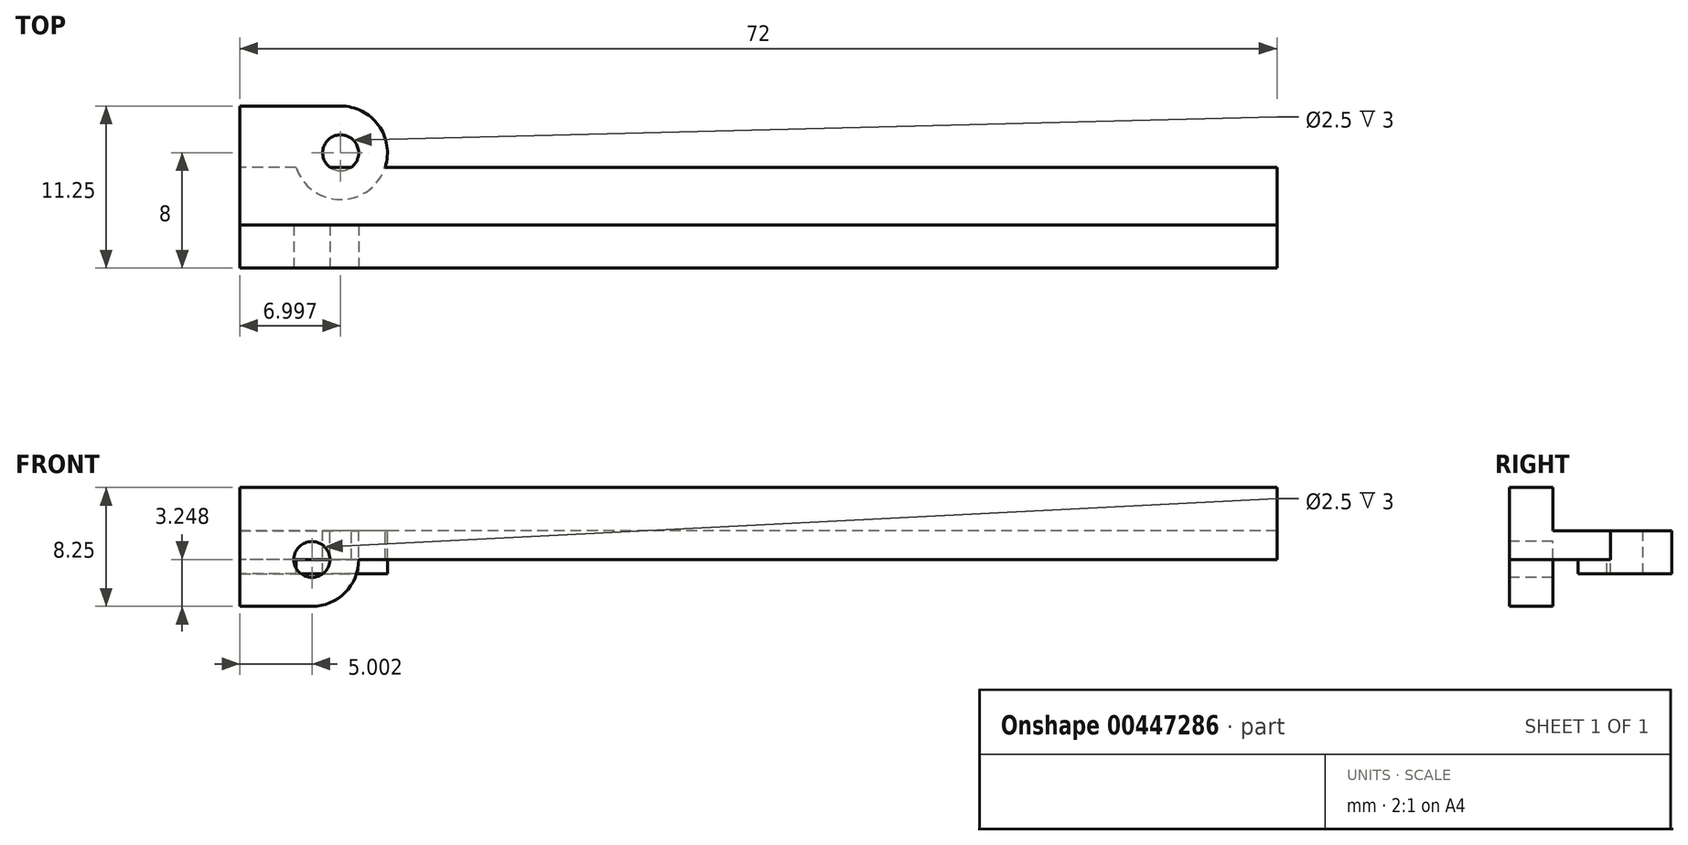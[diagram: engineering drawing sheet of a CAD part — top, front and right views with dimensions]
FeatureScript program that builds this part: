
annotation { "Feature Type Name" : "Feature", "Feature Type Description" : "" }
export const myFeature = defineFeature(function(context is Context, id is Id, definition is map)
    precondition{}
    {
        {
            var Q0;
            Q0=qCreatedBy(makeId("Front.planeOp"),FACE);
            var sketch = newSketch(context, id + "F0", { "sketchPlane" : qUnion([Q0])});
            skLineSegment(sketch, "E0", {"start": v(-25.69, -103.36) * mm, "end": v(-25.69, 66.64) * mm, "construction": true});
            skLineSegment(sketch, "E1.bottom", {"start": v(-27.99, 69.24) * mm, "end": v(16.71, 69.24) * mm, "construction": true});
            skLineSegment(sketch, "E1.top", {"start": v(-27.99, -89.76) * mm, "end": v(16.71, -89.76) * mm, "construction": true});
            skLineSegment(sketch, "E1.left", {"start": v(-27.99, 69.24) * mm, "end": v(-27.99, -89.76) * mm, "construction": true});
            skLineSegment(sketch, "E1.right", {"start": v(16.71, 69.24) * mm, "end": v(16.71, -89.76) * mm, "construction": true});
            skLineSegment(sketch, "E2", {"start": v(-25.69, 66.64) * mm, "end": v(-25.69, 76.64) * mm, "construction": true});
            skLineSegment(sketch, "E3", {"start": v(-25.69, 76.64) * mm, "end": v(-38.69, 76.64) * mm});
            skLineSegment(sketch, "E4", {"start": v(-38.69, 76.64) * mm, "end": v(-38.69, 79.64) * mm});
            skLineSegment(sketch, "E5", {"start": v(-38.69, 79.64) * mm, "end": v(33.31, 79.64) * mm});
            skLineSegment(sketch, "E6", {"start": v(-33.69, 79.64) * mm, "end": v(-33.69, 74.64) * mm, "construction": true});
            skCircle(sketch, "E7", {"center": v(-33.69, 74.64) * mm, "radius": 1.25 * mm});
            skCircle(sketch, "E8", {"center": v(-33.69, 74.64) * mm, "radius": 3.25 * mm});
            skLineSegment(sketch, "E9", {"start": v(-33.69, 71.39) * mm, "end": v(-38.69, 71.39) * mm});
            skLineSegment(sketch, "E10", {"start": v(-38.69, 71.39) * mm, "end": v(-38.69, 76.64) * mm});
            skLineSegment(sketch, "E11", {"start": v(-25.69, 76.64) * mm, "end": v(33.31, 76.64) * mm});
            skLineSegment(sketch, "E12", {"start": v(33.31, 76.64) * mm, "end": v(33.31, 79.64) * mm});
            skLineSegment(sketch, "E13", {"start": v(33.31, 76.64) * mm, "end": v(33.31, 74.64) * mm});
            skLineSegment(sketch, "E14", {"start": v(33.31, 74.64) * mm, "end": v(-30.44, 74.64) * mm});
            skLineSegment(sketch, "E15", {"start": v(33.31, 74.64) * mm, "end": v(33.31, 72.64) * mm});
            skLineSegment(sketch, "E16", {"start": v(33.31, 72.64) * mm, "end": v(-31.13, 72.64) * mm});
            skSolve(sketch);
        }
        {
            var Q0;
            {var subQ0=sQuery(id+"F0.wireOp",EDGE,"E11");Q0=makeQuery(id+"F0.imprint","IMPRINT",FACE,{"disambiguationData":[TD([[makeQuery(id+"F0.imprint","IMPRINT",EDGE,{"derivedFrom":subQ0}),-1.0]])]});}
            var Q1;
            Q1=makeQuery(id+"F0.imprint","IMPRINT",FACE,{"disambiguationData":[TD([[makeQuery(id+"F0.imprint","IMPRINT",EDGE,{"derivedFrom":sQuery(id+"F0.wireOp",EDGE,"E7")}),-1.0]])]});
            var Q2;
            {var subQ4=sQuery(id+"F0.wireOp",EDGE,"E9");Q2=makeQuery(id+"F0.imprint","IMPRINT",FACE,{"disambiguationData":[TD([[makeQuery(id+"F0.imprint","IMPRINT",EDGE,{"derivedFrom":subQ4}),-1.0]])]});}
            var Q3;
            {var subQ0=sQuery(id+"F0.wireOp",EDGE,"E4");Q3=makeQuery(id+"F0.imprint","IMPRINT",FACE,{"disambiguationData":[TD([[makeQuery(id+"F0.imprint","IMPRINT",EDGE,{"derivedFrom":subQ0}),-1.0]])]});}
            var Q4;
            {var subQ0=sQuery(id+"F0.wireOp",EDGE,"E8");var subQ1=sQuery(id+"F0.wireOp",EDGE,"E3");var subQ2=makeQuery(id+"F0.imprint","INTERSECT",VERTEX,{"disambiguationData":[OD(0.0)],"derivedFrom":[subQ1,subQ0]});Q4=makeQuery(id+"F0.imprint","IMPRINT",FACE,{"disambiguationData":[TD([[makeQuery(id+"F0.imprint","IMPRINT",EDGE,{"disambiguationData":[TD([[subQ2,-1.0]])],"derivedFrom":subQ1}),-1.0]])]});}
            extrude(context, id + "F1", {"entities" : qUnion([Q0, Q1, Q2, Q3, Q4]), "oppositeDirection" : true, "depth" : 3 * mm});
        }
        {
            var Q0;
            Q0=makeQuery(id+"F1.opExtrude","CAP_FACE",FACE,{"disambiguationData":[OSD([sQuery(id+"F0.wireOp",EDGE,"E4"),sQuery(id+"F0.wireOp",EDGE,"E5"),sQuery(id+"F0.wireOp",EDGE,"E7"),sQuery(id+"F0.wireOp",EDGE,"E8"),sQuery(id+"F0.wireOp",EDGE,"E9"),sQuery(id+"F0.wireOp",EDGE,"E10"),sQuery(id+"F0.wireOp",EDGE,"E12"),sQuery(id+"F0.wireOp",EDGE,"E13"),sQuery(id+"F0.wireOp",EDGE,"E14")])],"isStart":false});
            var sketch = newSketch(context, id + "F2", { "sketchPlane" : qUnion([Q0])});
            skLineSegment(sketch, "E17.bottom", {"start": v(-33.31, 74.64) * mm, "end": v(38.69, 74.64) * mm});
            skLineSegment(sketch, "E17.top", {"start": v(-33.31, 76.64) * mm, "end": v(38.69, 76.64) * mm});
            skLineSegment(sketch, "E17.left", {"start": v(-33.31, 74.64) * mm, "end": v(-33.31, 76.64) * mm});
            skLineSegment(sketch, "E17.right", {"start": v(38.69, 74.64) * mm, "end": v(38.69, 76.64) * mm});
            skSolve(sketch);
        }
        {
            var Q0;
            Q0 = qSketchRegion(id + "F2", true);
            extrude(context, id + "F3", {"entities" : qUnion([Q0]), "operationType" : NewBodyOperationType.ADD, "depth" : 4 * mm});
        }
        {
            var Q0;
            Q0=makeQuery(id+"F3.opExtrude","SWEPT_FACE",FACE,{"disambiguationData":[OSD([sQuery(id+"F2.wireOp",EDGE,"E17.top")])]});
            var sketch = newSketch(context, id + "F4", { "sketchPlane" : qUnion([Q0])});
            skLineSegment(sketch, "E18", {"start": v(-31.7, 3) * mm, "end": v(-31.7, 8) * mm, "construction": true});
            skCircle(sketch, "E19", {"center": v(-31.7, 8) * mm, "radius": 1.25 * mm});
            skCircle(sketch, "E20", {"center": v(-31.7, 8) * mm, "radius": 3.25 * mm});
            skLineSegment(sketch, "E21", {"start": v(-38.69, 7) * mm, "end": v(-38.69, 11.25) * mm});
            skLineSegment(sketch, "E22", {"start": v(-38.69, 11.25) * mm, "end": v(-31.7, 11.25) * mm});
            skSolve(sketch);
        }
        {
            var Q0;
            {var subQ5=sQuery(id+"F4.wireOp",EDGE,"E21");Q0=makeQuery(id+"F4.imprint","IMPRINT",FACE,{"disambiguationData":[TD([[makeQuery(id+"F4.imprint","IMPRINT",EDGE,{"derivedFrom":subQ5}),-1.0]])]});}
            var Q1;
            {var subQ2=makeQuery(id+"F3.opExtrude","CAP_EDGE",EDGE,{"disambiguationData":[OSD([sQuery(id+"F2.wireOp",EDGE,"E17.top")])],"isStart":false});var subQ4=sQuery(id+"F4.wireOp",EDGE,"E19");var subQ5=makeQuery(id+"F4.imprint","INTERSECT",VERTEX,{"disambiguationData":[OD(0.0)],"derivedFrom":[subQ2,subQ4]});Q1=makeQuery(id+"F4.imprint","IMPRINT",FACE,{"disambiguationData":[TD([[makeQuery(id+"F4.imprint","IMPRINT",EDGE,{"disambiguationData":[TD([[subQ5,-1.0]])],"derivedFrom":subQ4}),-1.0]])]});}
            var Q2;
            {var subQ0=sQuery(id+"F4.wireOp",EDGE,"E19");var subQ1=makeQuery(id+"F3.opExtrude","CAP_EDGE",EDGE,{"disambiguationData":[OSD([sQuery(id+"F2.wireOp",EDGE,"E17.top")])],"isStart":false});var subQ2=makeQuery(id+"F4.imprint","INTERSECT",VERTEX,{"disambiguationData":[OD(0.0)],"derivedFrom":[subQ1,subQ0]});Q2=makeQuery(id+"F4.imprint","IMPRINT",FACE,{"disambiguationData":[TD([[makeQuery(id+"F4.imprint","IMPRINT",EDGE,{"disambiguationData":[TD([[subQ2,1.0]])],"derivedFrom":subQ0}),-1.0]])]});}
            extrude(context, id + "F5", {"entities" : qUnion([Q0, Q1, Q2]), "operationType" : NewBodyOperationType.ADD, "oppositeDirection" : true, "depth" : 3 * mm});
        }
    });
